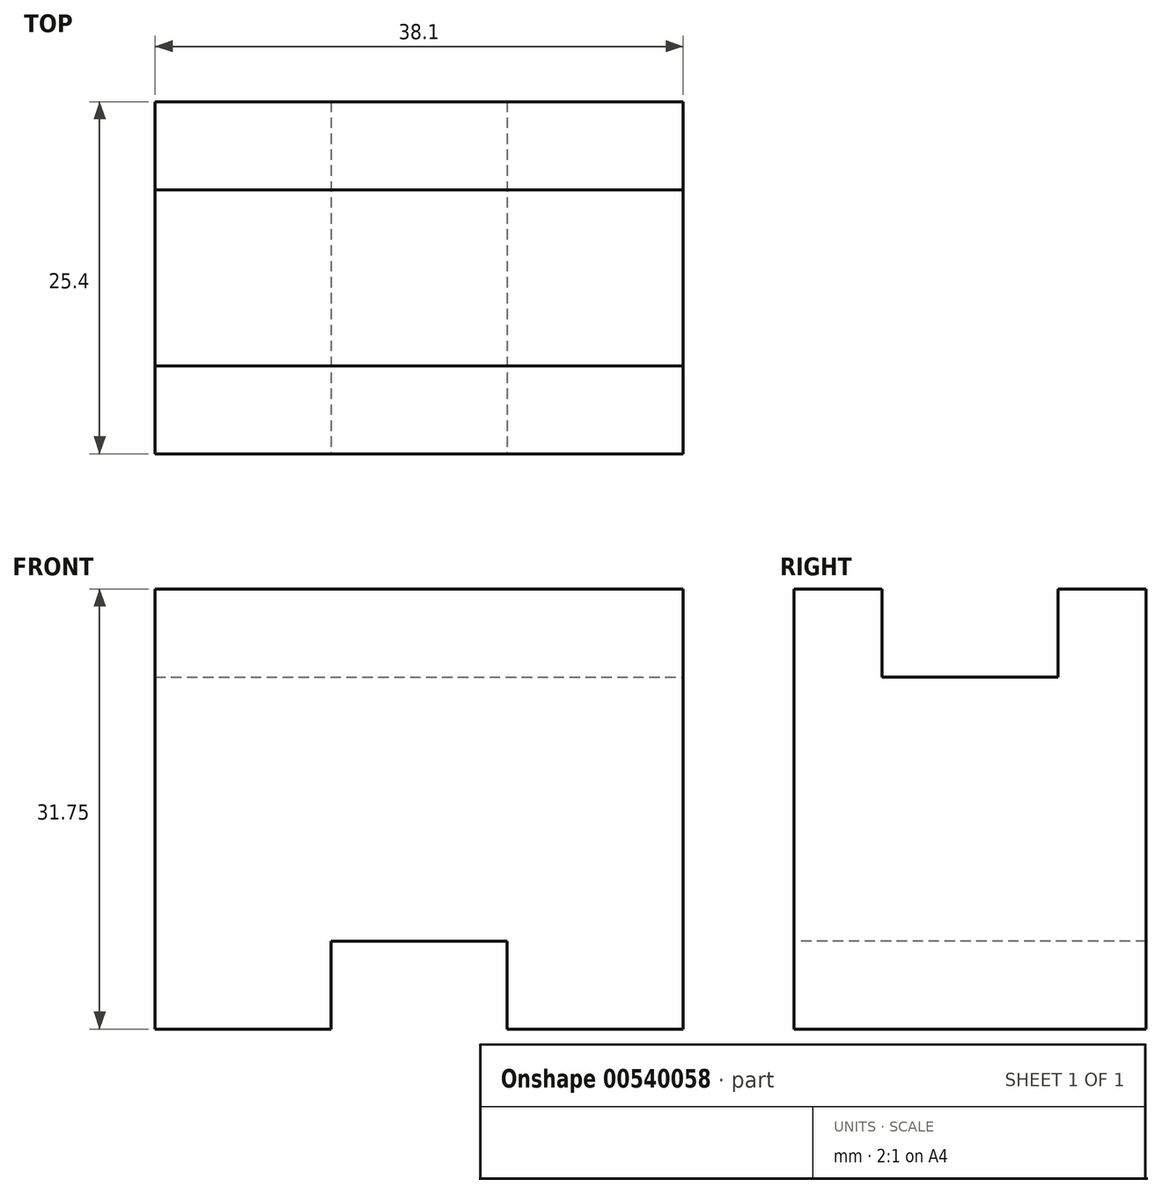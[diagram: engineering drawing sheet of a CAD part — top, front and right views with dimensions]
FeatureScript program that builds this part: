
annotation { "Feature Type Name" : "Feature", "Feature Type Description" : "" }
export const myFeature = defineFeature(function(context is Context, id is Id, definition is map)
    precondition{}
    {
        {
            var Q0;
            Q0=qCreatedBy(makeId("Right.planeOp"),FACE);
            var sketch = newSketch(context, id + "F0", { "sketchPlane" : qUnion([Q0])});
            skLineSegment(sketch, "E0", {"start": v(0, 0) * mm, "end": v(25.4, 0) * mm});
            skLineSegment(sketch, "E1", {"start": v(25.4, 0) * mm, "end": v(25.4, 31.75) * mm});
            skLineSegment(sketch, "E2", {"start": v(25.4, 31.75) * mm, "end": v(0, 31.75) * mm});
            skLineSegment(sketch, "E3", {"start": v(0, 31.75) * mm, "end": v(0, 0) * mm});
            skSolve(sketch);
        }
        {
            var Q0;
            Q0 = qSketchRegion(id + "F0", true);
            extrude(context, id + "F1", {"entities" : qUnion([Q0]), "oppositeDirection" : true, "depth" : 38.1 * mm, "offsetDistance" : 25.4 * mm});
        }
        {
            var Q0;
            Q0=makeQuery(id+"F1.opExtrude","SWEPT_FACE",FACE,{"disambiguationData":[OSD([sQuery(id+"F0.wireOp",EDGE,"E2")])]});
            var sketch = newSketch(context, id + "F2", { "sketchPlane" : qUnion([Q0])});
            skLineSegment(sketch, "E4", {"start": v(-38.1, 25.4) * mm, "end": v(-38.1, 19.05) * mm});
            skLineSegment(sketch, "E5", {"start": v(-38.1, 19.05) * mm, "end": v(0, 19.05) * mm});
            skLineSegment(sketch, "E6", {"start": v(0, 12.7) * mm, "end": v(-0.41, 12.7) * mm});
            skPoint(sketch, "E7.end.orphan", {"position": v(-38.1, 12.7) * mm});
            skLineSegment(sketch, "E8", {"start": v(-38.1, 19.05) * mm, "end": v(-38.1, 6.35) * mm});
            skLineSegment(sketch, "E9", {"start": v(-38.1, 6.35) * mm, "end": v(0, 6.35) * mm});
            skLineSegment(sketch, "E10", {"start": v(0, 19.05) * mm, "end": v(0, 6.35) * mm});
            skSolve(sketch);
        }
        {
            var Q0;
            Q0 = qSketchRegion(id + "F2", true);
            extrude(context, id + "F3", {"entities" : qUnion([Q0]), "operationType" : NewBodyOperationType.REMOVE, "oppositeDirection" : true, "depth" : 6.35 * mm, "offsetDistance" : 25.4 * mm});
        }
        {
            var Q0;
            Q0=makeQuery(id+"F1.opExtrude","SWEPT_FACE",FACE,{"disambiguationData":[OSD([sQuery(id+"F0.wireOp",EDGE,"E3")])]});
            var sketch = newSketch(context, id + "F4", { "sketchPlane" : qUnion([Q0])});
            skLineSegment(sketch, "E11", {"start": v(-38.1, 0) * mm, "end": v(-25.4, 0) * mm});
            skLineSegment(sketch, "E12", {"start": v(-25.4, 0) * mm, "end": v(-25.4, 6.35) * mm});
            skLineSegment(sketch, "E13", {"start": v(-25.4, 6.35) * mm, "end": v(-12.7, 6.35) * mm});
            skLineSegment(sketch, "E14", {"start": v(-12.7, 6.35) * mm, "end": v(-12.7, 0) * mm});
            skLineSegment(sketch, "E15", {"start": v(-25.4, 0) * mm, "end": v(-12.7, 0) * mm});
            skSolve(sketch);
        }
        {
            var Q0;
            Q0 = qSketchRegion(id + "F4", true);
            extrude(context, id + "F5", {"entities" : qUnion([Q0]), "operationType" : NewBodyOperationType.REMOVE, "oppositeDirection" : true, "depth" : 25.4 * mm, "offsetDistance" : 25.4 * mm});
        }
    });
